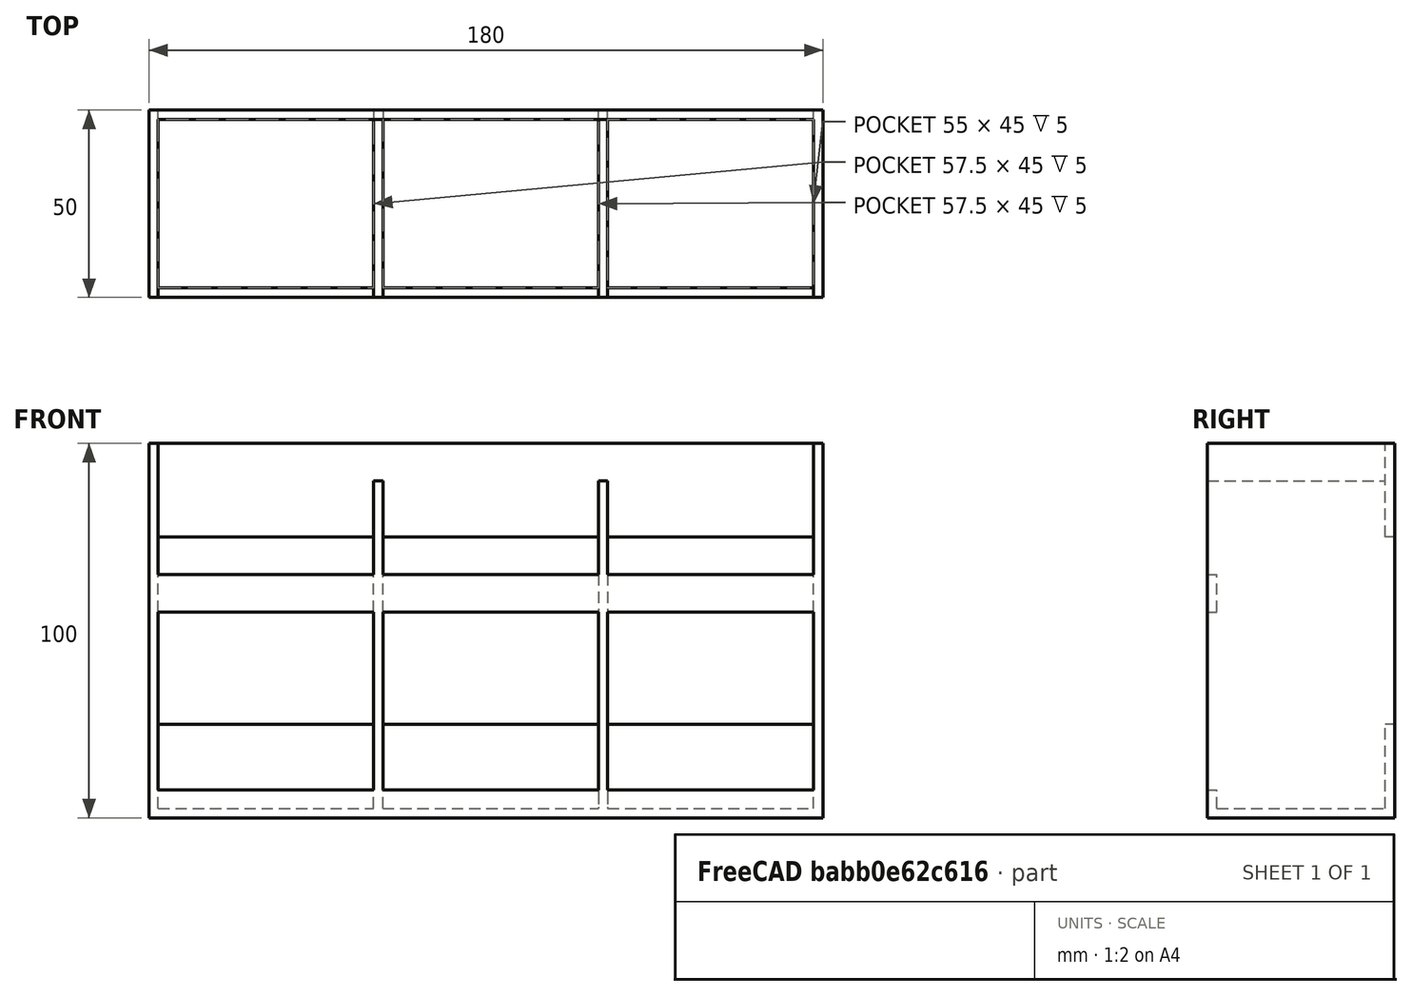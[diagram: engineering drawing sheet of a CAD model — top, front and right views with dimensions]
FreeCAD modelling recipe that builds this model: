
FCSTD DOCUMENT  (FreeCAD 0.18R16117 (Git))
Label: Toothbrush_Holder
License: All rights reserved
LicenseURL: http://en.wikipedia.org/wiki/All_rights_reserved
objects: Part::Box×8, Part::Cut×2, Part::MultiFuse×1
note: 11 computed .brp shape members not serialized (recipe doc carries the construction recipe); baked Part::Feature solids carry a one-line shape summary decoded from their .brp

FEATURE [Part::Box] Box  label="Shell"
  AttacherType = Attacher::AttachEngine3D
  Height = 100
  Length = 180
  Width = 50
FEATURE [Part::Box] Box001  label="Shell Cutout"
  AttacherType = Attacher::AttachEngine3D
  Height = 97.5
  Length = 175
  Placement = pos=(2.5,0,2.5) rot=(0,0,1;0rad)
  Width = 47.5
FEATURE [Part::Box] Box002  label="Center Divider"
  AttacherType = Attacher::AttachEngine3D
  Height = 87.5
  Length = 2.5
  Placement = pos=(60,0,2.5) rot=(0,0,1;0rad)
  Width = 50
FEATURE [Part::Box] Box003  label="Front Bar"
  AttacherType = Attacher::AttachEngine3D
  Height = 10
  Length = 175
  Placement = pos=(2.5,0,55) rot=(0,0,1;0rad)
  Width = 2.5
FEATURE [Part::Cut] Cut  label="Hollow Shell"
  Base = -> Box
  Tool = -> Box001
FEATURE [Part::Box] Box004  label="Bottom Lip"
  AttacherType = Attacher::AttachEngine3D
  Height = 5
  Length = 175
  Placement = pos=(2.5,0,2.5) rot=(0,0,1;0rad)
  Width = 2.5
FEATURE [Part::Box] Box005  label="Back Cutout"
  AttacherType = Attacher::AttachEngine3D
  Height = 50
  Length = 175
  Placement = pos=(2.5,47.5,25) rot=(0,0,1;0rad)
  Width = 2.5
FEATURE [Part::Cut] Cut001  label="Outer Shell"
  Base = -> Cut
  Tool = -> Box005
FEATURE [Part::Box] Box006  label="Right Divider"
  AttacherType = Attacher::AttachEngine3D
  Height = 87.5
  Length = 2.5
  Placement = pos=(120,0,2.5) rot=(0,0,1;0rad)
  Width = 50
FEATURE [Part::Box] Box007  label="Left Divider"
  AttacherType = Attacher::AttachEngine3D
  Height = 87.5
  Length = 2.5
  Placement = pos=(60,0,2.5) rot=(0,0,1;0rad)
  Width = 50
FEATURE [Part::MultiFuse] Fusion
  Shapes = -> [Box007,Cut001,Box002,Box003,Box004,Box006]
